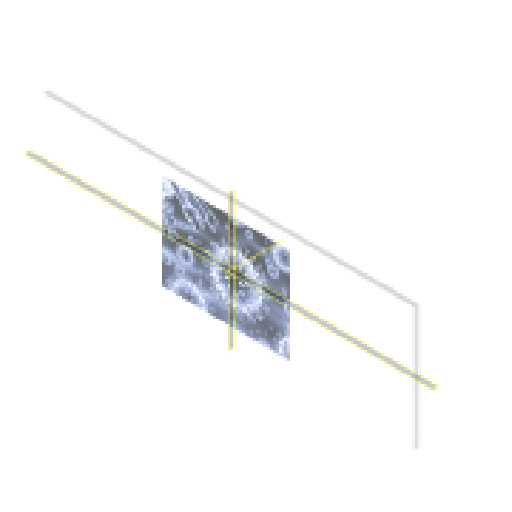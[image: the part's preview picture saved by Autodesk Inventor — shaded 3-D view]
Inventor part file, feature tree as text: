
AUTODESK INVENTOR PART (.ipt)
format: ipt  version: 2024.1 (Build 281209000, 209)  size: 4,366,848 bytes
history: native  units: mm
features: other x3, sketch x2, plane x2, extrude x1
ambient origin geometry x8: Origin, YZ Plane, XZ Plane, XY Plane, X Axis, Y Axis, Z Axis, Center Point
bodies: Solid1 (feature_tree)
feature tree (8):
  extrude  "Extrusion1"  Depth=25.0mm
  other  "Decal1"
  other  "Arbeitsachse1"
  sketch  "Sketch1"  dims[d0=75.0mm d1=25.0mm]
  sketch  "Sketch2"  dims[d2=1.0mm d3=0.0mm]
  other  "Image2"
  plane  "Arbeitsebene1"
  plane  "Arbeitsebene2"
